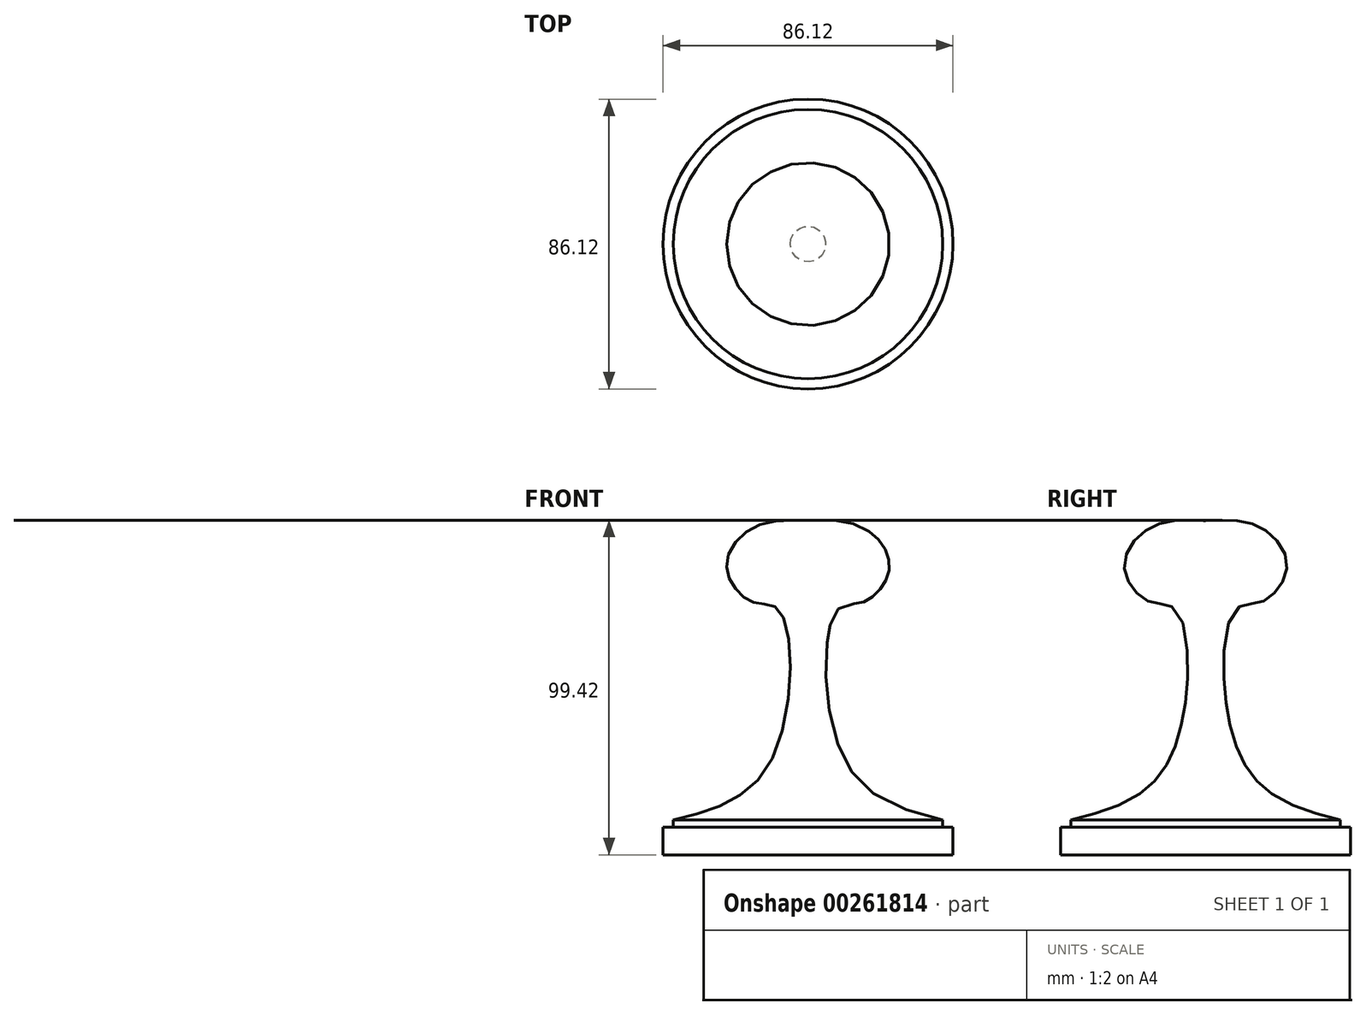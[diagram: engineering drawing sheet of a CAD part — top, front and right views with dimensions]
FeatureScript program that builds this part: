
annotation { "Feature Type Name" : "Feature", "Feature Type Description" : "" }
export const myFeature = defineFeature(function(context is Context, id is Id, definition is map)
    precondition{}
    {
        {
            var Q0;
            Q0=qCreatedBy(makeId("Front.planeOp"),FACE);
            var sketch = newSketch(context, id + "F0", { "sketchPlane" : qUnion([Q0])});
            skLineSegment(sketch, "E0", {"start": v(0, 63.77) * mm, "end": v(0, -63.07) * mm});
            skLineSegment(sketch, "E1", {"start": v(0, -55.3) * mm, "end": v(-43.06, -55.3) * mm});
            skLineSegment(sketch, "E2", {"start": v(-43.06, -55.3) * mm, "end": v(-43.06, -47.06) * mm});
            skLineSegment(sketch, "E3", {"start": v(-43.06, -47.06) * mm, "end": v(-40, -47.06) * mm});
            skLineSegment(sketch, "E4", {"start": v(-40, -47.06) * mm, "end": v(-40, -44.95) * mm});
            skFitSpline(sketch, "E5", {"points": [v(-40, -44.95) * mm, v(-11.06, -27.53) * mm, v(-8.47, 17.18) * mm, v(-15.53, 19.53) * mm, v(-21.89, 24.24) * mm, v(-24, 32.47) * mm, v(-16, 42.12) * mm, v(0, 44) * mm], "startDerivative": vector(167.64, 42.15) * mm, "endDerivative": vector(121.5, -4.32) * mm});
            skSolve(sketch);
        }
        {
            var Q0;
            {var subQ0=sQuery(id+"F0.wireOp",EDGE,"E1");Q0=makeQuery(id+"F0.imprint","IMPRINT",FACE,{"disambiguationData":[TD([[makeQuery(id+"F0.imprint","IMPRINT",EDGE,{"derivedFrom":subQ0}),-1.0]])]});}
            var Q1;
            Q1=sQuery(id+"F0.wireOp",EDGE,"E0");
            revolve(context, id + "F1", {"entities" : qUnion([Q0]), "axis" : qUnion([Q1]), "revolveType" : RevolveType.FULL});
        }
    });
